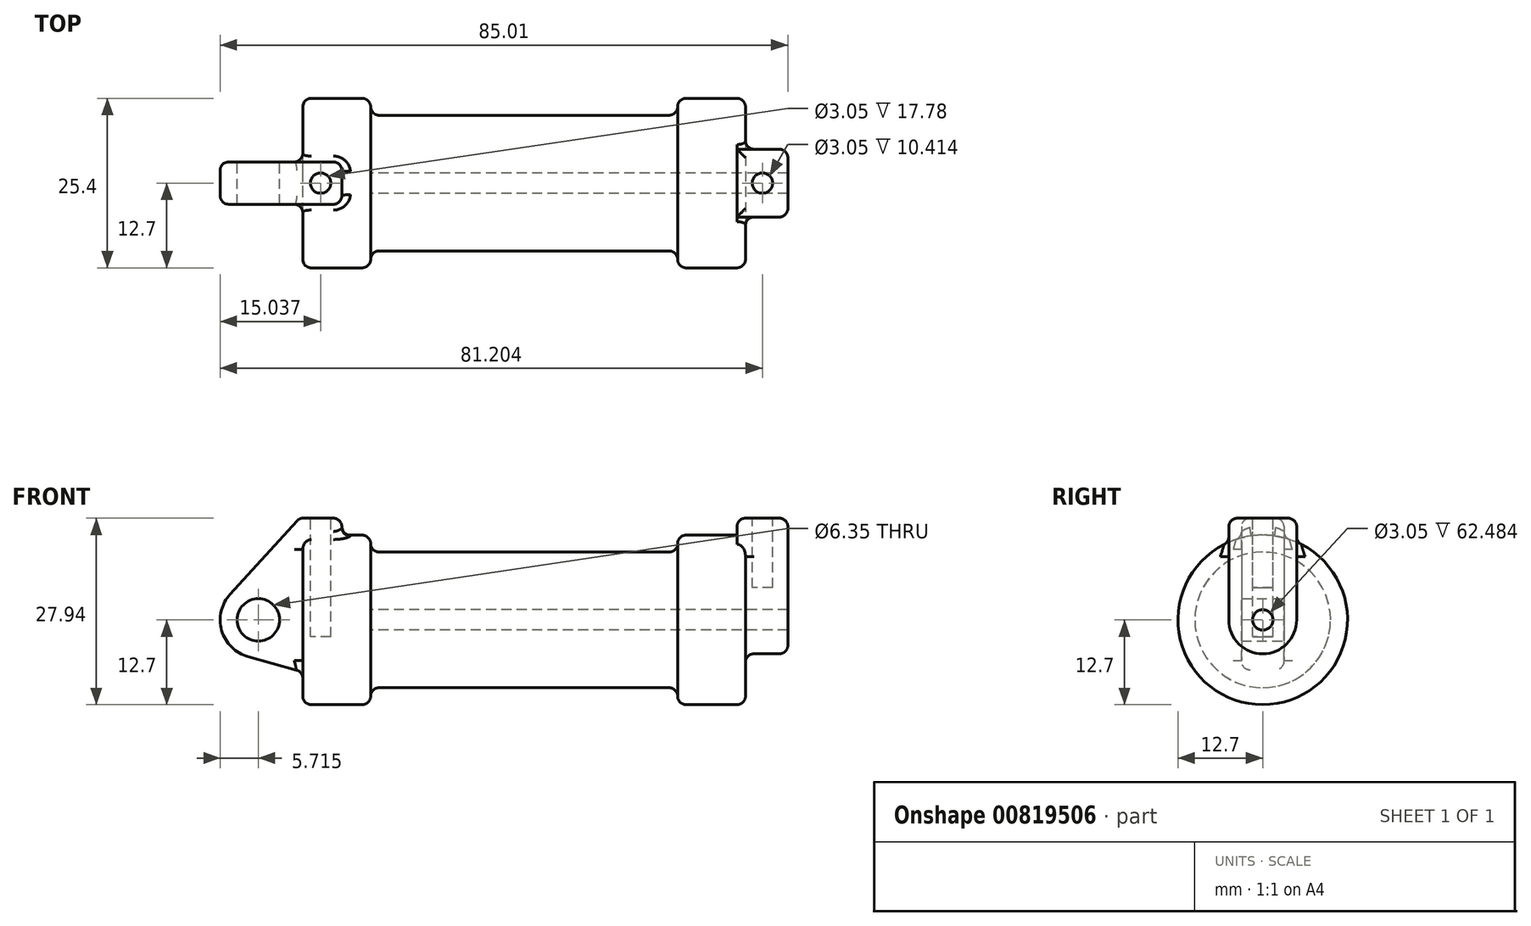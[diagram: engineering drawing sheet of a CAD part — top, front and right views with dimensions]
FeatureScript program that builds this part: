
annotation { "Feature Type Name" : "Feature", "Feature Type Description" : "" }
export const myFeature = defineFeature(function(context is Context, id is Id, definition is map)
    precondition{}
    {
        {
            var Q0;
            Q0=qCreatedBy(makeId("Front.planeOp"),FACE);
            var sketch = newSketch(context, id + "F0", { "sketchPlane" : qUnion([Q0])});
            skLineSegment(sketch, "E0", {"start": v(0, 0) * mm, "end": v(0, 12.7) * mm});
            skLineSegment(sketch, "E1", {"start": v(0, 12.7) * mm, "end": v(10.16, 12.7) * mm});
            skLineSegment(sketch, "E2", {"start": v(10.16, 12.7) * mm, "end": v(10.16, 10.16) * mm});
            skLineSegment(sketch, "E3", {"start": v(10.16, 10.16) * mm, "end": v(56.13, 10.16) * mm});
            skLineSegment(sketch, "E4", {"start": v(56.13, 10.16) * mm, "end": v(56.13, 12.7) * mm});
            skLineSegment(sketch, "E5", {"start": v(56.13, 12.7) * mm, "end": v(66.3, 12.7) * mm});
            skLineSegment(sketch, "E6", {"start": v(66.3, 12.7) * mm, "end": v(66.3, 0) * mm});
            skLineSegment(sketch, "E7", {"start": v(66.3, 0) * mm, "end": v(0, 0) * mm});
            skLineSegment(sketch, "E8", {"start": v(5.84, 15.24) * mm, "end": v(-0.5, 15.24) * mm});
            skLineSegment(sketch, "E9", {"start": v(-0.5, 15.24) * mm, "end": v(-10.88, 3.85) * mm});
            skLineSegment(sketch, "E10", {"start": v(0, 0) * mm, "end": v(-6.65, 0) * mm});
            skCircle(sketch, "E11", {"center": v(-6.65, 0) * mm, "radius": 5.72 * mm});
            skCircle(sketch, "E12", {"center": v(-6.65, 0) * mm, "radius": 3.18 * mm});
            skLineSegment(sketch, "E13", {"start": v(5.84, 15.24) * mm, "end": v(5.84, -9.4) * mm});
            skLineSegment(sketch, "E14", {"start": v(5.84, -9.4) * mm, "end": v(-8.18, -5.5) * mm});
            skSolve(sketch);
        }
        {
            var Q0;
            {var subQ0=sQuery(id+"F0.wireOp",EDGE,"E2");Q0=makeQuery(id+"F0.imprint","IMPRINT",FACE,{"disambiguationData":[TD([[makeQuery(id+"F0.imprint","IMPRINT",EDGE,{"derivedFrom":subQ0}),-1.0]])]});}
            var Q1;
            {var subQ0=sQuery(id+"F0.wireOp",EDGE,"E0");Q1=makeQuery(id+"F0.imprint","IMPRINT",FACE,{"disambiguationData":[TD([[makeQuery(id+"F0.imprint","IMPRINT",EDGE,{"derivedFrom":subQ0}),-1.0]])]});}
            var Q2;
            Q2=sQuery(id+"F0.wireOp",EDGE,"E7");
            revolve(context, id + "F1", {"entities" : qUnion([Q0, Q1]), "axis" : qUnion([Q2]), "revolveType" : RevolveType.FULL, "surfaceOperationType" : NewSurfaceOperationType.NEW});
        }
        {
            var Q0;
            {var subQ3=sQuery(id+"F0.wireOp",EDGE,"E0");Q0=makeQuery(id+"F0.imprint","IMPRINT",FACE,{"disambiguationData":[TD([[makeQuery(id+"F0.imprint","IMPRINT",EDGE,{"derivedFrom":subQ3}),1.0]])]});}
            var Q1;
            {var subQ4=sQuery(id+"F0.wireOp",EDGE,"E12");Q1=makeQuery(id+"F0.imprint","IMPRINT",FACE,{"disambiguationData":[TD([[makeQuery(id+"F0.imprint","IMPRINT",EDGE,{"derivedFrom":subQ4}),-1.0]])]});}
            var Q2;
            {var subQ0=sQuery(id+"F0.wireOp",EDGE,"E14");Q2=makeQuery(id+"F0.imprint","IMPRINT",FACE,{"disambiguationData":[TD([[makeQuery(id+"F0.imprint","IMPRINT",EDGE,{"derivedFrom":subQ0}),-1.0]])]});}
            var Q3;
            {var subQ0=sQuery(id+"F0.wireOp",EDGE,"E0");Q3=makeQuery(id+"F0.imprint","IMPRINT",FACE,{"disambiguationData":[TD([[makeQuery(id+"F0.imprint","IMPRINT",EDGE,{"derivedFrom":subQ0}),-1.0]])]});}
            extrude(context, id + "F2", {"entities" : qUnion([Q0, Q1, Q2, Q3]), "operationType" : NewBodyOperationType.ADD, "endBound" : BoundingType.SYMMETRIC, "depth" : 6.35 * mm});
        }
        {
            var Q0;
            Q0=makeQuery(id+"F1.opRevolve","SWEPT_FACE",FACE,{"disambiguationData":[OSD([sQuery(id+"F0.wireOp",EDGE,"E6")])]});
            var sketch = newSketch(context, id + "F3", { "sketchPlane" : qUnion([Q0])});
            skCircle(sketch, "E15", {"center": v(0, 0) * mm, "radius": 1.52 * mm});
            skCircle(sketch, "E16", {"center": v(0, 0) * mm, "radius": 5.08 * mm});
            skLineSegment(sketch, "E17", {"start": v(-5.08, 0) * mm, "end": v(-5.08, 15.24) * mm});
            skLineSegment(sketch, "E18", {"start": v(-5.08, 15.24) * mm, "end": v(5.08, 15.24) * mm});
            skLineSegment(sketch, "E19", {"start": v(5.08, 15.24) * mm, "end": v(5.08, 0) * mm});
            skSolve(sketch);
        }
        {
            var Q0;
            {var subQ0=sQuery(id+"F3.wireOp",EDGE,"E18");Q0=makeQuery(id+"F3.imprint","IMPRINT",FACE,{"disambiguationData":[TD([[makeQuery(id+"F3.imprint","IMPRINT",EDGE,{"derivedFrom":subQ0}),-1.0]])]});}
            extrude(context, id + "F4", {"entities" : qUnion([Q0]), "operationType" : NewBodyOperationType.ADD, "oppositeDirection" : true, "depth" : 1.27 * mm, "offsetDistance" : 25.4 * mm});
        }
        {
            var Q0;
            {var subQ0=sQuery(id+"F3.wireOp",EDGE,"E18");Q0=makeQuery(id+"F3.imprint","IMPRINT",FACE,{"disambiguationData":[TD([[makeQuery(id+"F3.imprint","IMPRINT",EDGE,{"derivedFrom":subQ0}),-1.0]])]});}
            var Q1;
            {var subQ0=sQuery(id+"F3.wireOp",EDGE,"E17");var subQ1=sQuery(id+"F3.wireOp",EDGE,"E16");var subQ2=makeQuery(id+"F3.imprint","INTERSECT",VERTEX,{"derivedFrom":[subQ1,subQ0]});Q1=makeQuery(id+"F3.imprint","IMPRINT",FACE,{"disambiguationData":[TD([[makeQuery(id+"F3.imprint","IMPRINT",EDGE,{"disambiguationData":[TD([[subQ2,1.0]])],"derivedFrom":subQ1}),-1.0]])]});}
            var Q2;
            Q2=makeQuery(id+"F3.imprint","IMPRINT",FACE,{"disambiguationData":[TD([[makeQuery(id+"F3.imprint","IMPRINT",EDGE,{"derivedFrom":sQuery(id+"F3.wireOp",EDGE,"E15")}),-1.0]])]});
            extrude(context, id + "F5", {"entities" : qUnion([Q0, Q1, Q2]), "operationType" : NewBodyOperationType.ADD, "depth" : 6.35 * mm, "offsetDistance" : 25.4 * mm});
        }
        {
            var Q0;
            Q0=makeQuery(id+"F3.imprint","IMPRINT",FACE,{"disambiguationData":[TD([[makeQuery(id+"F3.imprint","IMPRINT",EDGE,{"derivedFrom":sQuery(id+"F3.wireOp",EDGE,"E15")}),1.0]])]});
            var Q1;
            Q1=makeQuery(id+"F1.opRevolve","SWEPT_FACE",FACE,{"disambiguationData":[OSD([sQuery(id+"F0.wireOp",EDGE,"E2")])]});
            extrude(context, id + "F6", {"entities" : qUnion([Q0]), "operationType" : NewBodyOperationType.REMOVE, "endBound" : BoundingType.UP_TO_SURFACE, "oppositeDirection" : true, "endBoundEntityFace" : qUnion([Q1]), "depth" : 25.4 * mm});
        }
        {
            var Q0;
            Q0=makeQuery(id+"F2.opExtrude","SWEPT_FACE",FACE,{"disambiguationData":[OSD([sQuery(id+"F0.wireOp",EDGE,"E8")])]});
            var sketch = newSketch(context, id + "F7", { "sketchPlane" : qUnion([Q0])});
            skCircle(sketch, "E20", {"center": v(2.67, 0) * mm, "radius": 1.52 * mm});
            skPoint(sketch, "E20.centerSnap0", {"position": v(-0.5, 0) * mm});
            skPoint(sketch, "E20.centerSnap1", {"position": v(2.67, 3.18) * mm});
            skSolve(sketch);
        }
        {
            var Q0;
            Q0=qSketchRegion(id+"F7",true);
            extrude(context, id + "F8", {"entities" : qUnion([Q0]), "operationType" : NewBodyOperationType.REMOVE, "oppositeDirection" : true, "depth" : 17.78 * mm});
        }
        {
            var Q0;
            {var subQ0=sQuery(id+"F3.wireOp",EDGE,"E18");Q0=makeQuery(id+"F5.boolean.opBoolean","MERGE",FACE,{"derivedFrom":[makeQuery(id+"F4.opExtrude","SWEPT_FACE",FACE,{"disambiguationData":[OSD([subQ0])]}),makeQuery(id+"F5.opExtrude","SWEPT_FACE",FACE,{"disambiguationData":[OSD([subQ0])]})]});}
            var sketch = newSketch(context, id + "F9", { "sketchPlane" : qUnion([Q0])});
            skCircle(sketch, "E21", {"center": v(68.83, 0) * mm, "radius": 1.52 * mm});
            skPoint(sketch, "E21.centerSnap0", {"position": v(65.02, 0) * mm});
            skPoint(sketch, "E21.centerSnap1", {"position": v(68.83, 5.08) * mm});
            skSolve(sketch);
        }
        {
            var Q0;
            Q0=qSketchRegion(id+"F9",true);
            extrude(context, id + "F10", {"entities" : qUnion([Q0]), "operationType" : NewBodyOperationType.REMOVE, "oppositeDirection" : true, "depth" : 10.4 * mm});
        }
        {
            var Q0;
            Q0=makeQuery(id+"F1.opRevolve","SWEPT_EDGE",EDGE,{"disambiguationData":[OSD([sQuery(id+"F0.wireOp",EDGE,"E2"),sQuery(id+"F0.wireOp",EDGE,"E3")])]});
            var Q1;
            Q1=makeQuery(id+"F1.opRevolve","SWEPT_EDGE",EDGE,{"disambiguationData":[OSD([sQuery(id+"F0.wireOp",EDGE,"E1"),sQuery(id+"F0.wireOp",EDGE,"E2")])]});
            var Q2;
            Q2=makeQuery(id+"F1.opRevolve","SWEPT_EDGE",EDGE,{"disambiguationData":[OSD([sQuery(id+"F0.wireOp",EDGE,"E3"),sQuery(id+"F0.wireOp",EDGE,"E4")])]});
            var Q3;
            Q3=makeQuery(id+"F1.opRevolve","SWEPT_EDGE",EDGE,{"disambiguationData":[OSD([sQuery(id+"F0.wireOp",EDGE,"E4"),sQuery(id+"F0.wireOp",EDGE,"E5")])]});
            var Q4;
            Q4=makeQuery(id+"F1.opRevolve","SWEPT_EDGE",EDGE,{"disambiguationData":[OSD([sQuery(id+"F0.wireOp",EDGE,"E5"),sQuery(id+"F0.wireOp",EDGE,"E6")])]});
            var Q5;
            Q5=makeQuery(id+"F1.opRevolve","SWEPT_EDGE",EDGE,{"disambiguationData":[OSD([sQuery(id+"F0.wireOp",EDGE,"E0"),sQuery(id+"F0.wireOp",EDGE,"E1")])]});
            fillet(context, id + "F11", {"entities" : qUnion([Q0, Q1, Q2, Q3, Q4, Q5]), "radius" : 1.27 * mm, "tangentPropagation" : true, "allowEdgeOverflow" : false});
        }
        {
            var Q0;
            Q0=makeQuery(id+"F1.boolean.opBoolean","INTERSECT",EDGE,{"derivedFrom":[makeQuery(id+"F2.opExtrude","CAP_FACE",FACE,{"disambiguationData":[OSD([sQuery(id+"F0.wireOp",EDGE,"E8"),sQuery(id+"F0.wireOp",EDGE,"E9"),sQuery(id+"F0.wireOp",EDGE,"E11"),sQuery(id+"F0.wireOp",EDGE,"E12"),sQuery(id+"F0.wireOp",EDGE,"E13"),sQuery(id+"F0.wireOp",EDGE,"E14")])],"isStart":false}),makeQuery(id+"F1.opRevolve","SWEPT_FACE",FACE,{"disambiguationData":[OSD([sQuery(id+"F0.wireOp",EDGE,"E1")])]})]});
            var Q1;
            Q1=makeQuery(id+"F1.opRevolve","SWEPT_FACE",FACE,{"disambiguationData":[OSD([sQuery(id+"F0.wireOp",EDGE,"E0")])]});
            var Q2;
            Q2=makeQuery(id+"F2.opExtrude","CAP_EDGE",EDGE,{"disambiguationData":[OSD([sQuery(id+"F0.wireOp",EDGE,"E9")])],"isStart":true});
            var Q3;
            Q3=makeQuery(id+"F2.opExtrude","CAP_EDGE",EDGE,{"disambiguationData":[OSD([sQuery(id+"F0.wireOp",EDGE,"E9")])],"isStart":false});
            var Q4;
            Q4=makeQuery(id+"F5.opExtrude","CAP_EDGE",EDGE,{"disambiguationData":[OSD([sQuery(id+"F3.wireOp",EDGE,"E17")])],"isStart":true});
            var Q5;
            Q5=makeQuery(id+"F5.opExtrude","CAP_EDGE",EDGE,{"disambiguationData":[OSD([sQuery(id+"F3.wireOp",EDGE,"E17")])],"isStart":false});
            var Q6;
            {var subQ0=sQuery(id+"F3.wireOp",EDGE,"E18");var subQ1=sQuery(id+"F3.wireOp",EDGE,"E17");Q6=makeQuery(id+"F5.boolean.opBoolean","MERGE",EDGE,{"derivedFrom":[makeQuery(id+"F4.opExtrude","SWEPT_EDGE",EDGE,{"disambiguationData":[OSD([subQ1,subQ0])]}),makeQuery(id+"F5.opExtrude","SWEPT_EDGE",EDGE,{"disambiguationData":[OSD([subQ1,subQ0])]})]});}
            var Q7;
            {var subQ0=sQuery(id+"F3.wireOp",EDGE,"E19");var subQ1=sQuery(id+"F3.wireOp",EDGE,"E18");Q7=makeQuery(id+"F5.boolean.opBoolean","MERGE",EDGE,{"derivedFrom":[makeQuery(id+"F4.opExtrude","SWEPT_EDGE",EDGE,{"disambiguationData":[OSD([subQ1,subQ0])]}),makeQuery(id+"F5.opExtrude","SWEPT_EDGE",EDGE,{"disambiguationData":[OSD([subQ1,subQ0])]})]});}
            var Q8;
            Q8=makeQuery(id+"F4.opExtrude","CAP_EDGE",EDGE,{"disambiguationData":[OSD([sQuery(id+"F3.wireOp",EDGE,"E18")])],"isStart":false});
            var Q9;
            Q9=makeQuery(id+"F5.opExtrude","CAP_EDGE",EDGE,{"disambiguationData":[OSD([sQuery(id+"F3.wireOp",EDGE,"E18")])],"isStart":false});
            var Q10;
            Q10=makeQuery(id+"F2.opExtrude","CAP_EDGE",EDGE,{"disambiguationData":[OSD([sQuery(id+"F0.wireOp",EDGE,"E8")])],"isStart":false});
            var Q11;
            Q11=makeQuery(id+"F2.opExtrude","SWEPT_EDGE",EDGE,{"disambiguationData":[OSD([sQuery(id+"F0.wireOp",EDGE,"E8"),sQuery(id+"F0.wireOp",EDGE,"E9")])]});
            var Q12;
            Q12=makeQuery(id+"F2.opExtrude","CAP_EDGE",EDGE,{"disambiguationData":[OSD([sQuery(id+"F0.wireOp",EDGE,"E8")])],"isStart":true});
            var Q13;
            Q13=makeQuery(id+"F2.opExtrude","SWEPT_EDGE",EDGE,{"disambiguationData":[OSD([sQuery(id+"F0.wireOp",EDGE,"E8"),sQuery(id+"F0.wireOp",EDGE,"E13")])]});
            var Q14;
            Q14=makeQuery(id+"F2.opExtrude","SWEPT_FACE",FACE,{"disambiguationData":[OSD([sQuery(id+"F0.wireOp",EDGE,"E13")])]});
            var Q15;
            Q15=makeQuery(id+"F4.opExtrude","CAP_EDGE",EDGE,{"disambiguationData":[OSD([sQuery(id+"F0.wireOp",EDGE,"E5"),sQuery(id+"F0.wireOp",EDGE,"E6")])],"isStart":false});
            fillet(context, id + "F12", {"entities" : qUnion([Q0, Q1, Q2, Q3, Q4, Q5, Q6, Q7, Q8, Q9, Q10, Q11, Q12, Q13, Q14, Q15]), "radius" : 1.27 * mm, "tangentPropagation" : true, "allowEdgeOverflow" : false});
        }
    });
